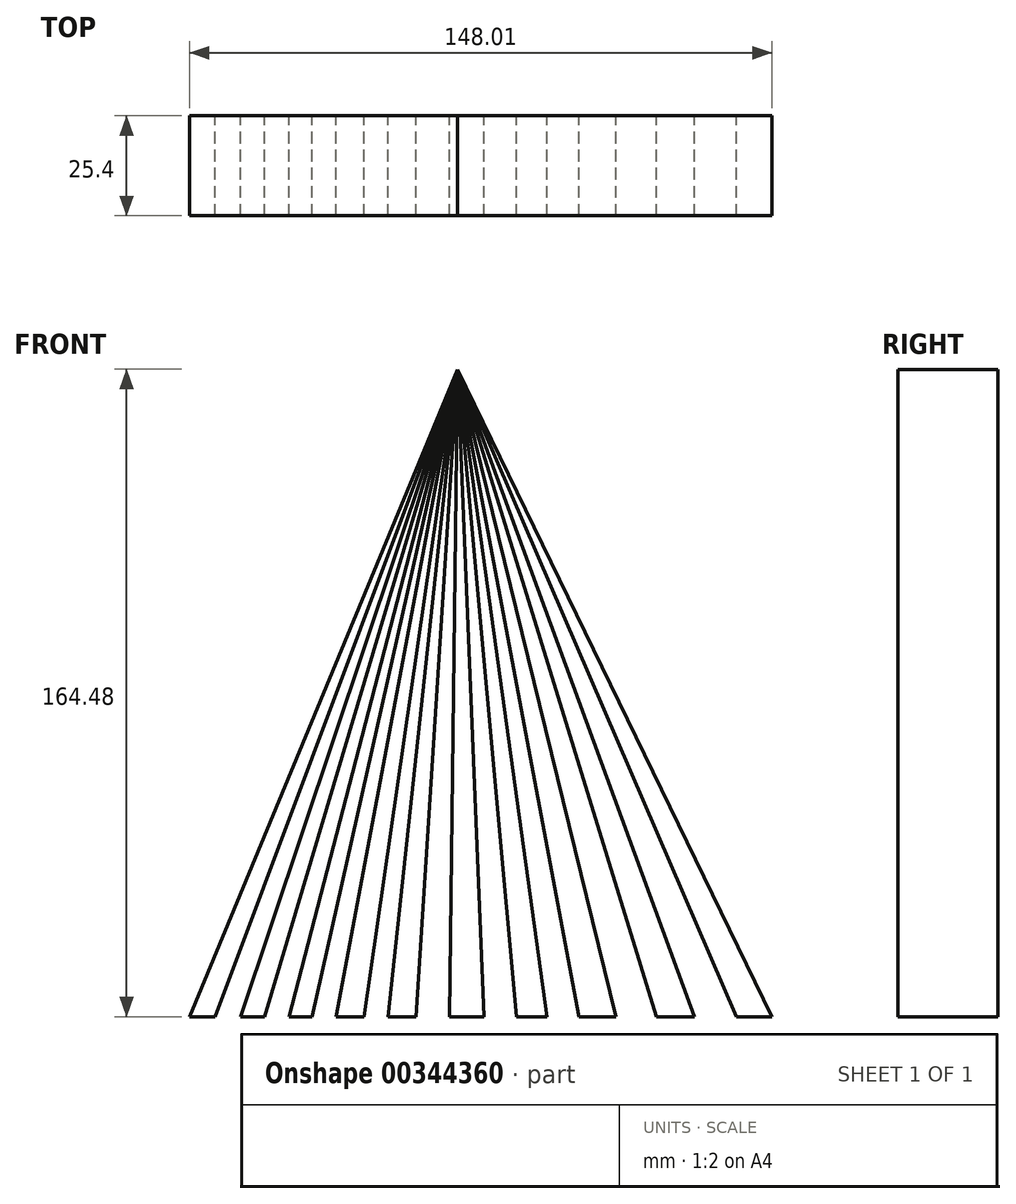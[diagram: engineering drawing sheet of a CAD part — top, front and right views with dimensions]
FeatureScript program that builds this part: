
annotation { "Feature Type Name" : "Feature", "Feature Type Description" : "" }
export const myFeature = defineFeature(function(context is Context, id is Id, definition is map)
    precondition{}
    {
        {
            var Q0;
            Q0=qCreatedBy(makeId("Front.planeOp"),FACE);
            var sketch = newSketch(context, id + "F0", { "sketchPlane" : qUnion([Q0])});
            skLineSegment(sketch, "E0", {"start": v(-97.64, 0) * mm, "end": v(57.12, 0) * mm});
            skLineSegment(sketch, "E1", {"start": v(-22.79, 164.48) * mm, "end": v(57.12, 0) * mm});
            skLineSegment(sketch, "E2", {"start": v(-22.79, 164.48) * mm, "end": v(48.03, 0) * mm});
            skLineSegment(sketch, "E3", {"start": v(-22.79, 164.48) * mm, "end": v(37.46, 0) * mm});
            skLineSegment(sketch, "E4", {"start": v(-22.79, 164.48) * mm, "end": v(27.77, 0) * mm});
            skLineSegment(sketch, "E5", {"start": v(-22.79, 164.48) * mm, "end": v(17.49, 0) * mm});
            skLineSegment(sketch, "E6", {"start": v(-22.79, 164.48) * mm, "end": v(8.09, 0) * mm});
            skLineSegment(sketch, "E7", {"start": v(-22.79, 164.48) * mm, "end": v(0, 0) * mm});
            skLineSegment(sketch, "E8", {"start": v(-22.79, 164.48) * mm, "end": v(-7.78, 0) * mm});
            skLineSegment(sketch, "E9", {"start": v(-22.79, 164.48) * mm, "end": v(-16, 0) * mm});
            skLineSegment(sketch, "E10", {"start": v(-22.79, 164.48) * mm, "end": v(-24.81, 0) * mm});
            skLineSegment(sketch, "E11", {"start": v(-22.79, 164.48) * mm, "end": v(-33.33, 0) * mm});
            skLineSegment(sketch, "E12", {"start": v(-22.79, 164.48) * mm, "end": v(-40.38, 0) * mm});
            skLineSegment(sketch, "E13", {"start": v(-22.79, 164.48) * mm, "end": v(-46.55, 0) * mm});
            skLineSegment(sketch, "E14", {"start": v(-22.79, 164.48) * mm, "end": v(-53.6, 0) * mm});
            skLineSegment(sketch, "E15", {"start": v(-22.79, 164.48) * mm, "end": v(-59.77, 0) * mm});
            skLineSegment(sketch, "E16", {"start": v(-22.79, 164.48) * mm, "end": v(-65.64, 0) * mm});
            skLineSegment(sketch, "E17", {"start": v(-22.79, 164.48) * mm, "end": v(-71.81, 0) * mm});
            skLineSegment(sketch, "E18", {"start": v(-22.79, 164.48) * mm, "end": v(-77.97, 0) * mm});
            skLineSegment(sketch, "E19", {"start": v(-22.79, 164.48) * mm, "end": v(-84.43, 0) * mm});
            skLineSegment(sketch, "E20", {"start": v(-22.79, 164.48) * mm, "end": v(-90.89, 0) * mm});
            skLineSegment(sketch, "E21", {"start": v(-22.79, 164.48) * mm, "end": v(-97.64, 0) * mm});
            skSolve(sketch);
        }
        {
            var Q0;
            {var subQ0=sQuery(id+"F0.wireOp",EDGE,"kIVc3crD-qLV6-1tZP-Zr7l-U2CTwt1xw3KY");Q0=makeQuery(id+"F0.imprint","IMPRINT",FACE,{"disambiguationData":[TD([[makeQuery(id+"F0.imprint","IMPRINT",EDGE,{"derivedFrom":subQ0}),-1.0]])]});}
            var Q1;
            {var subQ0=sQuery(id+"F0.wireOp",EDGE,"E19");Q1=makeQuery(id+"F0.imprint","IMPRINT",FACE,{"disambiguationData":[TD([[makeQuery(id+"F0.imprint","IMPRINT",EDGE,{"derivedFrom":subQ0}),-1.0]])]});}
            var Q2;
            {var subQ0=sQuery(id+"F0.wireOp",EDGE,"E17");Q2=makeQuery(id+"F0.imprint","IMPRINT",FACE,{"disambiguationData":[TD([[makeQuery(id+"F0.imprint","IMPRINT",EDGE,{"derivedFrom":subQ0}),-1.0]])]});}
            var Q3;
            {var subQ0=sQuery(id+"F0.wireOp",EDGE,"E15");Q3=makeQuery(id+"F0.imprint","IMPRINT",FACE,{"disambiguationData":[TD([[makeQuery(id+"F0.imprint","IMPRINT",EDGE,{"derivedFrom":subQ0}),-1.0]])]});}
            var Q4;
            {var subQ0=sQuery(id+"F0.wireOp",EDGE,"E13");Q4=makeQuery(id+"F0.imprint","IMPRINT",FACE,{"disambiguationData":[TD([[makeQuery(id+"F0.imprint","IMPRINT",EDGE,{"derivedFrom":subQ0}),-1.0]])]});}
            var Q5;
            {var subQ0=sQuery(id+"F0.wireOp",EDGE,"E11");Q5=makeQuery(id+"F0.imprint","IMPRINT",FACE,{"disambiguationData":[TD([[makeQuery(id+"F0.imprint","IMPRINT",EDGE,{"derivedFrom":subQ0}),-1.0]])]});}
            var Q6;
            {var subQ0=sQuery(id+"F0.wireOp",EDGE,"E9");Q6=makeQuery(id+"F0.imprint","IMPRINT",FACE,{"disambiguationData":[TD([[makeQuery(id+"F0.imprint","IMPRINT",EDGE,{"derivedFrom":subQ0}),-1.0]])]});}
            var Q7;
            {var subQ0=sQuery(id+"F0.wireOp",EDGE,"E7");Q7=makeQuery(id+"F0.imprint","IMPRINT",FACE,{"disambiguationData":[TD([[makeQuery(id+"F0.imprint","IMPRINT",EDGE,{"derivedFrom":subQ0}),-1.0]])]});}
            var Q8;
            {var subQ0=sQuery(id+"F0.wireOp",EDGE,"E5");Q8=makeQuery(id+"F0.imprint","IMPRINT",FACE,{"disambiguationData":[TD([[makeQuery(id+"F0.imprint","IMPRINT",EDGE,{"derivedFrom":subQ0}),-1.0]])]});}
            var Q9;
            {var subQ0=sQuery(id+"F0.wireOp",EDGE,"E3");Q9=makeQuery(id+"F0.imprint","IMPRINT",FACE,{"disambiguationData":[TD([[makeQuery(id+"F0.imprint","IMPRINT",EDGE,{"derivedFrom":subQ0}),-1.0]])]});}
            var Q10;
            {var subQ0=sQuery(id+"F0.wireOp",EDGE,"E1");Q10=makeQuery(id+"F0.imprint","IMPRINT",FACE,{"disambiguationData":[TD([[makeQuery(id+"F0.imprint","IMPRINT",EDGE,{"derivedFrom":subQ0}),-1.0]])]});}
            extrude(context, id + "F1", {"entities" : qUnion([Q0, Q1, Q2, Q3, Q4, Q5, Q6, Q7, Q8, Q9, Q10]), "depth" : 25.4 * mm});
        }
    });
